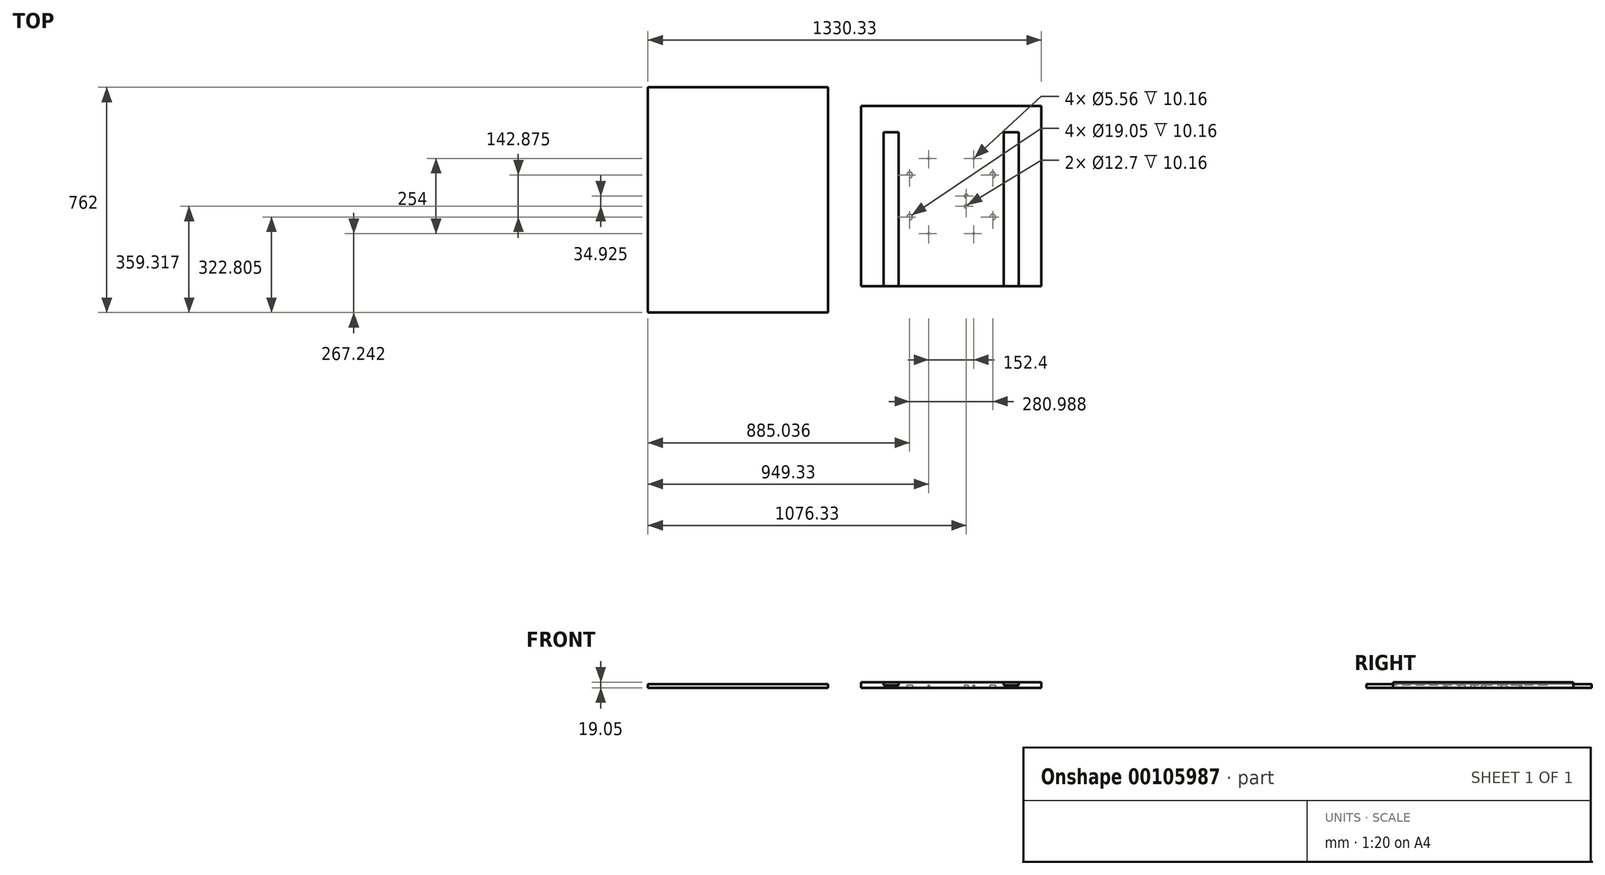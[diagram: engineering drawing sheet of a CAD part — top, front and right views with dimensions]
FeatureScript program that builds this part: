
annotation { "Feature Type Name" : "Feature", "Feature Type Description" : "" }
export const myFeature = defineFeature(function(context is Context, id is Id, definition is map)
    precondition{}
    {
        {
            var Q0;
            Q0=qCreatedBy(makeId("Top.planeOp"),FACE);
            var sketch = newSketch(context, id + "F0", { "sketchPlane" : qUnion([Q0])});
            skLineSegment(sketch, "E0.bottom", {"start": v(-298.75, 396.01) * mm, "end": v(310.85, 396.01) * mm});
            skLineSegment(sketch, "E0.top", {"start": v(-298.75, -365.99) * mm, "end": v(310.85, -365.99) * mm});
            skLineSegment(sketch, "E0.left", {"start": v(-298.75, 396.01) * mm, "end": v(-298.75, -365.99) * mm});
            skLineSegment(sketch, "E0.right", {"start": v(310.85, 396.01) * mm, "end": v(310.85, -365.99) * mm});
            skLineSegment(sketch, "E1.bottom", {"start": v(421.98, 333.05) * mm, "end": v(1031.58, 333.05) * mm});
            skLineSegment(sketch, "E1.top", {"start": v(421.98, -276.55) * mm, "end": v(1031.58, -276.55) * mm});
            skLineSegment(sketch, "E1.left", {"start": v(421.98, 333.05) * mm, "end": v(421.98, -276.55) * mm});
            skLineSegment(sketch, "E1.right", {"start": v(1031.58, 333.05) * mm, "end": v(1031.58, -276.55) * mm});
            skSolve(sketch);
        }
        {
            var Q0;
            Q0=makeQuery(id+"F0.imprint","IMPRINT",FACE,{"disambiguationData":[TD([[makeQuery(id+"F0.imprint","IMPRINT",EDGE,{"derivedFrom":sQuery(id+"F0.wireOp",EDGE,"E0.bottom")}),-1.0]])]});
            extrude(context, id + "F1", {"entities" : qUnion([Q0]), "depth" : 12.7 * mm});
        }
        {
            var Q0;
            Q0=makeQuery(id+"F0.imprint","IMPRINT",FACE,{"disambiguationData":[TD([[makeQuery(id+"F0.imprint","IMPRINT",EDGE,{"derivedFrom":sQuery(id+"F0.wireOp",EDGE,"E1.bottom")}),-1.0]])]});
            extrude(context, id + "F2", {"entities" : qUnion([Q0]), "depth" : 7.94 * mm});
        }
        {
            var Q0;
            Q0=makeQuery(id+"F2.opExtrude","CAP_FACE",FACE,{"disambiguationData":[OSD([sQuery(id+"F0.wireOp",EDGE,"E1.bottom"),sQuery(id+"F0.wireOp",EDGE,"E1.top"),sQuery(id+"F0.wireOp",EDGE,"E1.left"),sQuery(id+"F0.wireOp",EDGE,"E1.right")])],"isStart":false});
            var sketch = newSketch(context, id + "F3", { "sketchPlane" : qUnion([Q0])});
            skLineSegment(sketch, "E2", {"start": v(498.18, 333.05) * mm, "end": v(498.18, -276.55) * mm, "construction": true});
            skLineSegment(sketch, "E3", {"start": v(955.38, 333.05) * mm, "end": v(955.38, -276.55) * mm, "construction": true});
            skLineSegment(sketch, "E4", {"start": v(421.98, 244.15) * mm, "end": v(1031.58, 244.15) * mm, "construction": true});
            skLineSegment(sketch, "E5", {"start": v(548.98, 333.05) * mm, "end": v(548.98, -276.55) * mm, "construction": true});
            skLineSegment(sketch, "E6", {"start": v(904.58, 333.05) * mm, "end": v(904.58, -276.55) * mm, "construction": true});
            skLineSegment(sketch, "E7", {"start": v(498.18, -276.55) * mm, "end": v(498.18, 244.15) * mm});
            skLineSegment(sketch, "E8", {"start": v(498.18, 244.15) * mm, "end": v(548.98, 244.15) * mm});
            skLineSegment(sketch, "E9", {"start": v(548.98, 244.15) * mm, "end": v(548.98, -276.55) * mm});
            skLineSegment(sketch, "E10", {"start": v(904.58, -276.55) * mm, "end": v(904.58, 244.15) * mm});
            skLineSegment(sketch, "E11", {"start": v(904.58, 244.15) * mm, "end": v(955.38, 244.15) * mm});
            skLineSegment(sketch, "E12", {"start": v(955.38, 244.15) * mm, "end": v(955.38, -276.55) * mm});
            skSolve(sketch);
        }
        {
            var Q0;
            {var subQ2=sQuery(id+"F3.wireOp",EDGE,"E7");Q0=makeQuery(id+"F3.imprint","IMPRINT",FACE,{"disambiguationData":[TD([[makeQuery(id+"F3.imprint","IMPRINT",EDGE,{"derivedFrom":subQ2}),1.0]])]});}
            extrude(context, id + "F4", {"entities" : qUnion([Q0]), "operationType" : NewBodyOperationType.ADD, "depth" : 11.1 * mm});
        }
        {
            var Q0;
            Q0=makeQuery(id+"F2.opExtrude","CAP_FACE",FACE,{"disambiguationData":[OSD([sQuery(id+"F0.wireOp",EDGE,"E1.bottom"),sQuery(id+"F0.wireOp",EDGE,"E1.top"),sQuery(id+"F0.wireOp",EDGE,"E1.left"),sQuery(id+"F0.wireOp",EDGE,"E1.right")])],"isStart":true});
            var sketch = newSketch(context, id + "F5", { "sketchPlane" : qUnion([Q0])});
            skLineSegment(sketch, "E13", {"start": v(574.38, 276.55) * mm, "end": v(574.38, -333.05) * mm, "construction": true});
            skLineSegment(sketch, "E14", {"start": v(421.98, -180.65) * mm, "end": v(1031.58, -180.65) * mm, "construction": true});
            skLineSegment(sketch, "E15", {"start": v(879.18, 276.55) * mm, "end": v(879.18, -333.05) * mm, "construction": true});
            skLineSegment(sketch, "E16", {"start": v(1031.58, 124.15) * mm, "end": v(421.98, 124.15) * mm, "construction": true});
            skLineSegment(sketch, "E17", {"start": v(726.78, 276.55) * mm, "end": v(726.78, -333.05) * mm, "construction": true});
            skLineSegment(sketch, "E18", {"start": v(421.98, -28.25) * mm, "end": v(1031.58, -28.25) * mm, "construction": true});
            skLineSegment(sketch, "E19.MirrorCS", {"start": v(1031.58, -28.25) * mm, "end": v(421.98, -28.25) * mm, "construction": true});
            skCircle(sketch, "E20", {"center": v(650.58, -155.25) * mm, "radius": 2.78 * mm});
            skCircle(sketch, "E21.MirrorC", {"center": v(802.98, -155.25) * mm, "radius": 2.78 * mm});
            skCircle(sketch, "E22.MirrorC", {"center": v(650.58, 98.75) * mm, "radius": 2.78 * mm});
            skCircle(sketch, "E23.MirrorC", {"center": v(802.98, 98.75) * mm, "radius": 2.78 * mm});
            skCircle(sketch, "E24", {"center": v(586.29, -99.69) * mm, "radius": 9.53 * mm});
            skCircle(sketch, "E25.MirrorC", {"center": v(867.27, -99.69) * mm, "radius": 9.53 * mm});
            skCircle(sketch, "E26.MirrorC", {"center": v(586.29, 43.19) * mm, "radius": 9.53 * mm});
            skCircle(sketch, "E27.MirrorC", {"center": v(867.27, 43.19) * mm, "radius": 9.53 * mm});
            skCircle(sketch, "E28", {"center": v(777.58, -28.25) * mm, "radius": 6.35 * mm});
            skLineSegment(sketch, "E29", {"start": v(777.58, -28.25) * mm, "end": v(777.58, 124.15) * mm, "construction": true});
            skCircle(sketch, "E30", {"center": v(777.58, 6.67) * mm, "radius": 6.35 * mm});
            skSolve(sketch);
        }
        {
            var Q0;
            Q0 = qSketchRegion(id + "F5", true);
            extrude(context, id + "F6", {"entities" : qUnion([Q0]), "operationType" : NewBodyOperationType.REMOVE, "oppositeDirection" : true, "depth" : 10.16 * mm});
        }
        {
            var Q0;
            {var subQ1=sQuery(id+"F0.wireOp",EDGE,"E1.top");var subQ3=sQuery(id+"F0.wireOp",EDGE,"E1.right");var subQ4=sQuery(id+"F3.wireOp",EDGE,"E7");var subQ5=sQuery(id+"F0.wireOp",EDGE,"E1.left");Q0=makeQuery(id+"F4.boolean.opBoolean","SPLIT",FACE,{"disambiguationData":[TD([makeQuery(id+"F4.opExtrude","SWEPT_FACE",FACE,{"disambiguationData":[OSD([subQ4])]})])],"derivedFrom":makeQuery(id+"F2.opExtrude","CAP_FACE",FACE,{"disambiguationData":[OSD([sQuery(id+"F0.wireOp",EDGE,"E1.bottom"),subQ1,subQ5,subQ3])],"isStart":false})});}
            var sketch = newSketch(context, id + "F7", { "sketchPlane" : qUnion([Q0])});
            skLineSegment(sketch, "E31", {"start": v(498.18, 212.4) * mm, "end": v(548.98, 212.4) * mm, "construction": true});
            skLineSegment(sketch, "E32", {"start": v(523.58, 212.4) * mm, "end": v(523.58, 244.15) * mm, "construction": true});
            skSolve(sketch);
        }
        {
            var Q0;
            {var subQ1=sQuery(id+"F3.wireOp",EDGE,"E10");var subQ2=sQuery(id+"F0.wireOp",EDGE,"E1.top");var subQ3=sQuery(id+"F0.wireOp",EDGE,"E1.left");var subQ5=sQuery(id+"F0.wireOp",EDGE,"E1.right");Q0=makeQuery(id+"F4.boolean.opBoolean","SPLIT",FACE,{"disambiguationData":[TD([makeQuery(id+"F4.opExtrude","SWEPT_FACE",FACE,{"disambiguationData":[OSD([subQ1])]})])],"derivedFrom":makeQuery(id+"F2.opExtrude","CAP_FACE",FACE,{"disambiguationData":[OSD([sQuery(id+"F0.wireOp",EDGE,"E1.bottom"),subQ2,subQ3,subQ5])],"isStart":false})});}
            var sketch = newSketch(context, id + "F8", { "sketchPlane" : qUnion([Q0])});
            skLineSegment(sketch, "E33", {"start": v(904.58, 212.4) * mm, "end": v(955.38, 212.4) * mm, "construction": true});
            skLineSegment(sketch, "E34", {"start": v(929.98, 212.4) * mm, "end": v(929.98, 244.15) * mm, "construction": true});
            skSolve(sketch);
        }
        {
            var Q0;
            Q0=makeQuery(id+"F1.opExtrude","CAP_FACE",FACE,{"disambiguationData":[OSD([sQuery(id+"F0.wireOp",EDGE,"E0.bottom"),sQuery(id+"F0.wireOp",EDGE,"E0.top"),sQuery(id+"F0.wireOp",EDGE,"E0.left"),sQuery(id+"F0.wireOp",EDGE,"E0.right")])],"isStart":true});
            var sketch = newSketch(context, id + "F9", { "sketchPlane" : qUnion([Q0])});
            skLineSegment(sketch, "E35", {"start": v(-197.15, 365.99) * mm, "end": v(-197.15, -396.01) * mm, "construction": true});
            skLineSegment(sketch, "E36", {"start": v(209.25, 365.99) * mm, "end": v(209.25, -396.01) * mm, "construction": true});
            skLineSegment(sketch, "E37", {"start": v(-298.75, 187.43) * mm, "end": v(310.85, 187.43) * mm, "construction": true});
            skLineSegment(sketch, "E38", {"start": v(6.05, 365.99) * mm, "end": v(6.05, -396.01) * mm, "construction": true});
            skLineSegment(sketch, "E39", {"start": v(-298.75, 354.86) * mm, "end": v(310.85, 354.86) * mm, "construction": true});
            skCircle(sketch, "E40", {"center": v(-197.15, 187.43) * mm, "radius": 1.27 * mm});
            skCircle(sketch, "E41", {"center": v(209.25, 187.43) * mm, "radius": 1.27 * mm});
            skCircle(sketch, "E42", {"center": v(6.05, 354.86) * mm, "radius": 1.27 * mm});
            skSolve(sketch);
        }
        {
            var Q0;
            Q0=makeQuery(id+"F2.opExtrude","CAP_FACE",FACE,{"disambiguationData":[OSD([sQuery(id+"F0.wireOp",EDGE,"E1.bottom"),sQuery(id+"F0.wireOp",EDGE,"E1.top"),sQuery(id+"F0.wireOp",EDGE,"E1.left"),sQuery(id+"F0.wireOp",EDGE,"E1.right")])],"isStart":true});
            var sketch = newSketch(context, id + "F10", { "sketchPlane" : qUnion([Q0])});
            skLineSegment(sketch, "E43", {"start": v(421.98, -321.93) * mm, "end": v(1031.58, -321.93) * mm, "construction": true});
            skLineSegment(sketch, "E44", {"start": v(726.78, -333.05) * mm, "end": v(726.78, -321.93) * mm, "construction": true});
            skCircle(sketch, "E45", {"center": v(726.78, -321.93) * mm, "radius": 1.27 * mm, "construction": true});
            skSolve(sketch);
        }
    });
